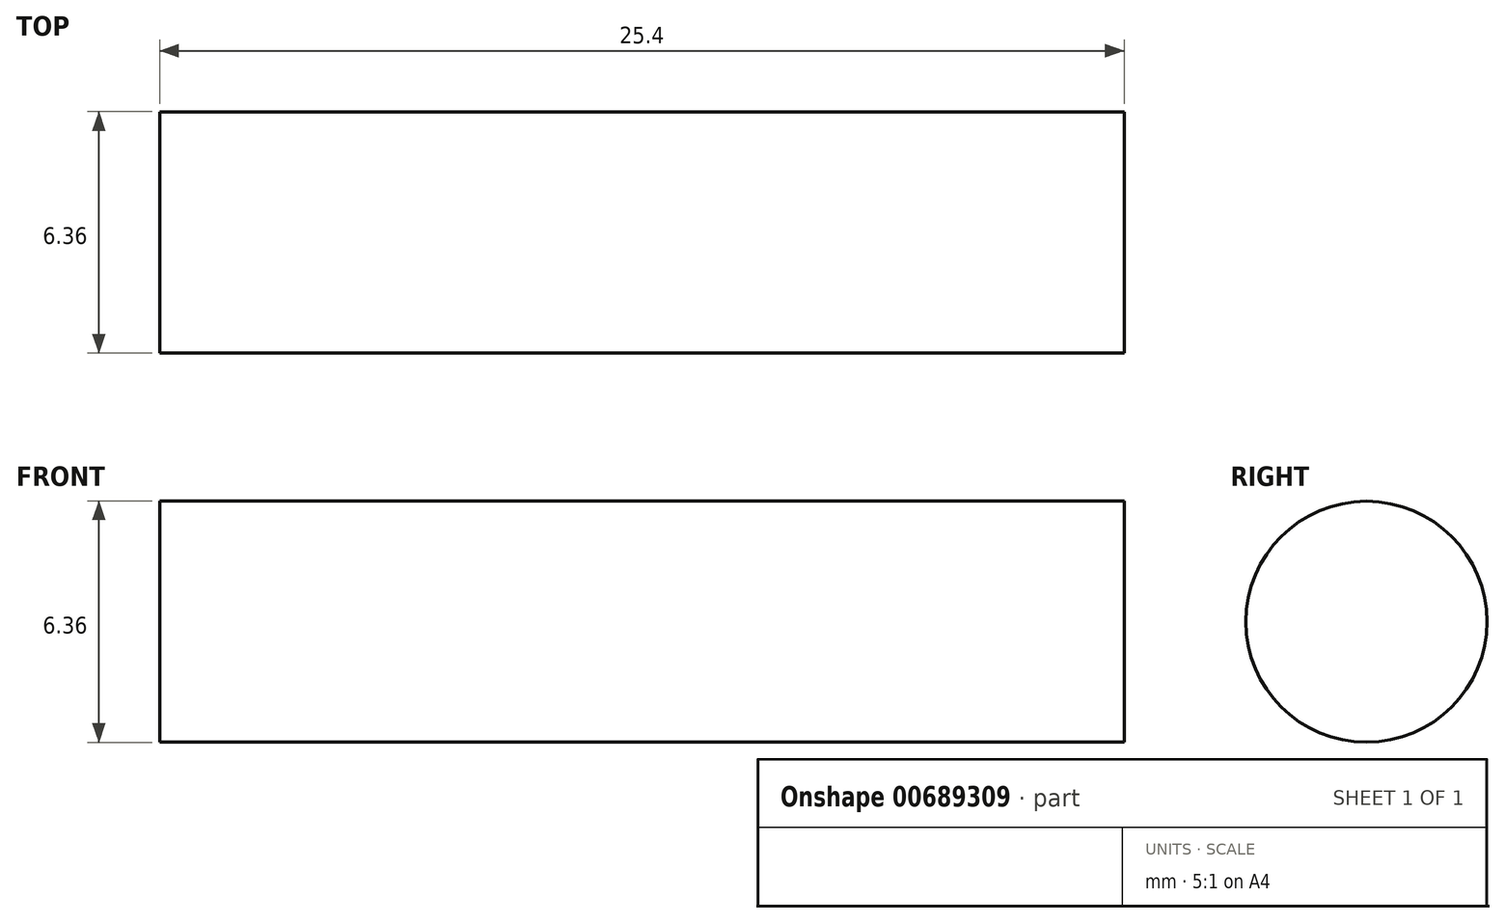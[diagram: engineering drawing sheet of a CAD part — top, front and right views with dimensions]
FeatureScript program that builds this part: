
annotation { "Feature Type Name" : "Feature", "Feature Type Description" : "" }
export const myFeature = defineFeature(function(context is Context, id is Id, definition is map)
    precondition{}
    {
        {
            var Q0;
            Q0=qCreatedBy(makeId("Right.planeOp"),FACE);
            var sketch = newSketch(context, id + "F0", { "sketchPlane" : qUnion([Q0])});
            skCircle(sketch, "E0", {"center": v(0, 0) * mm, "radius": 3.18 * mm});
            skSolve(sketch);
        }
        {
            var Q0;
            Q0 = qSketchRegion(id + "F0", true);
            extrude(context, id + "F1", {"entities" : qUnion([Q0]), "depth" : 25.4 * mm, "offsetDistance" : 25.4 * mm});
        }
    });
